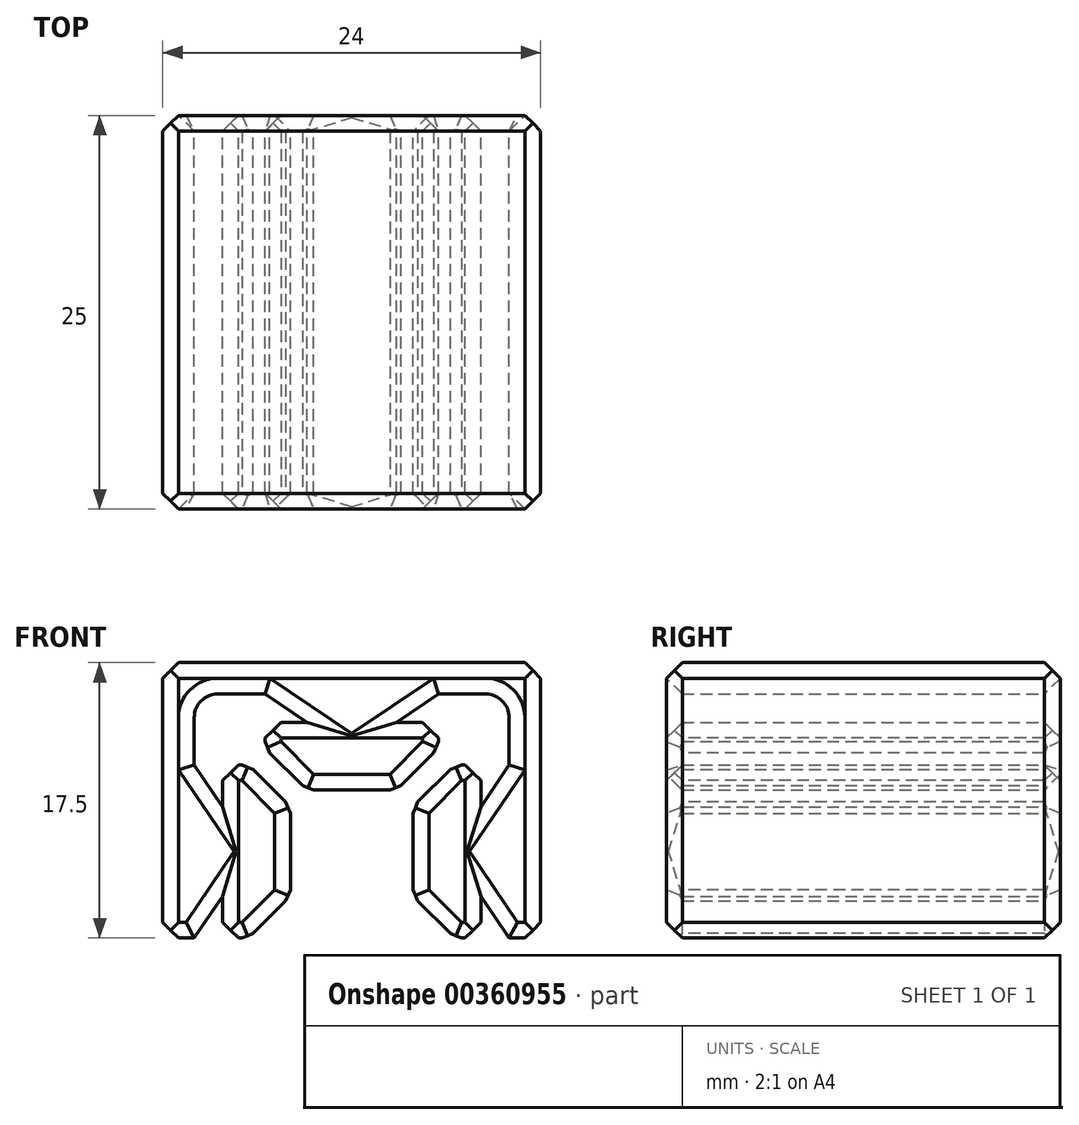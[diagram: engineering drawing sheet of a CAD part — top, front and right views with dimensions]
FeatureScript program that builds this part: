
annotation { "Feature Type Name" : "Feature", "Feature Type Description" : "" }
export const myFeature = defineFeature(function(context is Context, id is Id, definition is map)
    precondition{}
    {
        {
            var Q0;
            Q0=qCreatedBy(makeId("Front.planeOp"),FACE);
            var sketch = newSketch(context, id + "F0", { "sketchPlane" : qUnion([Q0])});
            skLineSegment(sketch, "E0", {"start": v(-8.2, 11) * mm, "end": v(-6.56, 11) * mm});
            skLineSegment(sketch, "E1", {"start": v(-6.56, 11) * mm, "end": v(-3.9, 8.34) * mm});
            skLineSegment(sketch, "E2", {"start": v(-3.9, 8.34) * mm, "end": v(-3.9, 2.66) * mm});
            skLineSegment(sketch, "E3", {"start": v(-3.9, 2.66) * mm, "end": v(-6.56, 0) * mm});
            skLineSegment(sketch, "E4", {"start": v(-6.56, 0) * mm, "end": v(-8.2, 0) * mm});
            skLineSegment(sketch, "E5", {"start": v(-8.2, 8.34) * mm, "end": v(-10, 11) * mm});
            skLineSegment(sketch, "E6", {"start": v(-8.2, 8.34) * mm, "end": v(-8.2, 11) * mm});
            skLineSegment(sketch, "E7", {"start": v(-8.2, 0) * mm, "end": v(-8.2, 2.66) * mm});
            skLineSegment(sketch, "E8", {"start": v(-8.2, 2.66) * mm, "end": v(-10, 0) * mm});
            skLineSegment(sketch, "E9.MirrorCS", {"start": v(8.2, 11) * mm, "end": v(6.56, 11) * mm});
            skLineSegment(sketch, "E10.MirrorCS", {"start": v(3.9, 8.34) * mm, "end": v(3.9, 2.66) * mm});
            skLineSegment(sketch, "E11.MirrorCS", {"start": v(8.2, 8.34) * mm, "end": v(10, 11) * mm});
            skLineSegment(sketch, "E12.MirrorCS", {"start": v(6.56, 0) * mm, "end": v(8.2, 0) * mm});
            skLineSegment(sketch, "E13.MirrorCS", {"start": v(3.9, 2.66) * mm, "end": v(6.56, 0) * mm});
            skLineSegment(sketch, "E14.MirrorCS", {"start": v(8.2, 0) * mm, "end": v(8.2, 2.66) * mm});
            skLineSegment(sketch, "E15.MirrorCS", {"start": v(6.56, 11) * mm, "end": v(3.9, 8.34) * mm});
            skLineSegment(sketch, "E16.MirrorCS", {"start": v(8.2, 8.34) * mm, "end": v(8.2, 11) * mm});
            skLineSegment(sketch, "E17.MirrorCS", {"start": v(8.2, 2.66) * mm, "end": v(10, 0) * mm});
            skLineSegment(sketch, "E18.MirrorCS", {"start": v(-5.5, 13.7) * mm, "end": v(-5.5, 12.06) * mm});
            skLineSegment(sketch, "E19.MirrorCS", {"start": v(-2.84, 9.4) * mm, "end": v(2.84, 9.4) * mm});
            skLineSegment(sketch, "E20.MirrorCS", {"start": v(-2.84, 13.7) * mm, "end": v(-5.5, 15.5) * mm});
            skLineSegment(sketch, "E21.MirrorCS", {"start": v(5.5, 12.06) * mm, "end": v(5.5, 13.7) * mm});
            skLineSegment(sketch, "E22.MirrorCS", {"start": v(2.84, 9.4) * mm, "end": v(5.5, 12.06) * mm});
            skLineSegment(sketch, "E23.MirrorCS", {"start": v(5.5, 13.7) * mm, "end": v(2.84, 13.7) * mm});
            skLineSegment(sketch, "E24.MirrorCS", {"start": v(-5.5, 12.06) * mm, "end": v(-2.84, 9.4) * mm});
            skLineSegment(sketch, "E25.MirrorCS", {"start": v(-2.84, 13.7) * mm, "end": v(-5.5, 13.7) * mm});
            skLineSegment(sketch, "E26.MirrorCS", {"start": v(2.84, 13.7) * mm, "end": v(5.5, 15.5) * mm});
            skPoint(sketch, "E27", {"position": v(0, 9.4) * mm});
            skPoint(sketch, "E28", {"position": v(0, 15.5) * mm});
            skLineSegment(sketch, "E29", {"start": v(-5.5, 15.5) * mm, "end": v(-8.5, 15.5) * mm});
            skLineSegment(sketch, "E30", {"start": v(-10, 14) * mm, "end": v(-10, 11) * mm});
            skLineSegment(sketch, "E31", {"start": v(5.5, 15.5) * mm, "end": v(8.5, 15.5) * mm});
            skLineSegment(sketch, "E32", {"start": v(10, 14) * mm, "end": v(10, 11) * mm});
            skPoint(sketch, "E33.visualSharp", {"position": v(-10, 15.5) * mm});
            skArc(sketch, "E33.filletArc", {"start": v(-8.5, 15.5) * mm, "mid": v(-9.56, 15.06) * mm, "end": v(-10, 14) * mm});
            skPoint(sketch, "E34.visualSharp", {"position": v(10, 15.5) * mm});
            skArc(sketch, "E34.filletArc", {"start": v(10, 14) * mm, "mid": v(9.56, 15.06) * mm, "end": v(8.5, 15.5) * mm});
            skLineSegment(sketch, "E35", {"start": v(-10, 0) * mm, "end": v(-12, 0) * mm});
            skLineSegment(sketch, "E36", {"start": v(-12, 0) * mm, "end": v(-12, 16) * mm});
            skLineSegment(sketch, "E37", {"start": v(-10.5, 17.5) * mm, "end": v(10.5, 17.5) * mm});
            skLineSegment(sketch, "E38", {"start": v(12, 16) * mm, "end": v(12, 0) * mm});
            skLineSegment(sketch, "E39", {"start": v(12, 0) * mm, "end": v(10, 0) * mm});
            skPoint(sketch, "E40.visualSharp", {"position": v(-12, 17.5) * mm});
            skPoint(sketch, "E41.visualSharp", {"position": v(12, 17.5) * mm});
            skLineSegment(sketch, "E42", {"start": v(-12, 16) * mm, "end": v(-12, 17.5) * mm});
            skLineSegment(sketch, "E43", {"start": v(-10.5, 17.5) * mm, "end": v(-12, 17.5) * mm});
            skLineSegment(sketch, "E44", {"start": v(10.5, 17.5) * mm, "end": v(12, 17.5) * mm});
            skLineSegment(sketch, "E45", {"start": v(12, 16) * mm, "end": v(12, 17.5) * mm});
            skSolve(sketch);
        }
        {
            var Q0;
            Q0=qSketchRegion(id+"F0",true);
            extrude(context, id + "F1", {"entities" : qUnion([Q0]), "depth" : 25 * mm});
        }
        {
            var Q0;
            Q0=makeQuery(id+"F1.opExtrude","CAP_FACE",FACE,{"disambiguationData":[OSD([sQuery(id+"F0.wireOp",EDGE,"E0"),sQuery(id+"F0.wireOp",EDGE,"E1"),sQuery(id+"F0.wireOp",EDGE,"E2"),sQuery(id+"F0.wireOp",EDGE,"E3"),sQuery(id+"F0.wireOp",EDGE,"E4"),sQuery(id+"F0.wireOp",EDGE,"E5"),sQuery(id+"F0.wireOp",EDGE,"E6"),sQuery(id+"F0.wireOp",EDGE,"E7"),sQuery(id+"F0.wireOp",EDGE,"E8"),sQuery(id+"F0.wireOp",EDGE,"E9.MirrorCS"),sQuery(id+"F0.wireOp",EDGE,"E10.MirrorCS"),sQuery(id+"F0.wireOp",EDGE,"E11.MirrorCS"),sQuery(id+"F0.wireOp",EDGE,"E12.MirrorCS"),sQuery(id+"F0.wireOp",EDGE,"E13.MirrorCS"),sQuery(id+"F0.wireOp",EDGE,"E14.MirrorCS"),sQuery(id+"F0.wireOp",EDGE,"E15.MirrorCS"),sQuery(id+"F0.wireOp",EDGE,"E16.MirrorCS"),sQuery(id+"F0.wireOp",EDGE,"E17.MirrorCS"),sQuery(id+"F0.wireOp",EDGE,"E18.MirrorCS"),sQuery(id+"F0.wireOp",EDGE,"E19.MirrorCS"),sQuery(id+"F0.wireOp",EDGE,"E20.MirrorCS"),sQuery(id+"F0.wireOp",EDGE,"E21.MirrorCS"),sQuery(id+"F0.wireOp",EDGE,"E22.MirrorCS"),sQuery(id+"F0.wireOp",EDGE,"E23.MirrorCS"),sQuery(id+"F0.wireOp",EDGE,"E24.MirrorCS"),sQuery(id+"F0.wireOp",EDGE,"E25.MirrorCS"),sQuery(id+"F0.wireOp",EDGE,"E26.MirrorCS"),sQuery(id+"F0.wireOp",EDGE,"E29"),sQuery(id+"F0.wireOp",EDGE,"E30"),sQuery(id+"F0.wireOp",EDGE,"E31"),sQuery(id+"F0.wireOp",EDGE,"E32"),sQuery(id+"F0.wireOp",EDGE,"E33.filletArc"),sQuery(id+"F0.wireOp",EDGE,"E34.filletArc"),sQuery(id+"F0.wireOp",EDGE,"E35"),sQuery(id+"F0.wireOp",EDGE,"E36"),sQuery(id+"F0.wireOp",EDGE,"E37"),sQuery(id+"F0.wireOp",EDGE,"E38"),sQuery(id+"F0.wireOp",EDGE,"E39"),sQuery(id+"F0.wireOp",EDGE,"E40.filletArc"),sQuery(id+"F0.wireOp",EDGE,"E41.filletArc")])],"isStart":false});
            var Q1;
            Q1=makeQuery(id+"F1.opExtrude","CAP_FACE",FACE,{"disambiguationData":[OSD([sQuery(id+"F0.wireOp",EDGE,"E0"),sQuery(id+"F0.wireOp",EDGE,"E1"),sQuery(id+"F0.wireOp",EDGE,"E2"),sQuery(id+"F0.wireOp",EDGE,"E3"),sQuery(id+"F0.wireOp",EDGE,"E4"),sQuery(id+"F0.wireOp",EDGE,"E5"),sQuery(id+"F0.wireOp",EDGE,"E6"),sQuery(id+"F0.wireOp",EDGE,"E7"),sQuery(id+"F0.wireOp",EDGE,"E8"),sQuery(id+"F0.wireOp",EDGE,"E9.MirrorCS"),sQuery(id+"F0.wireOp",EDGE,"E10.MirrorCS"),sQuery(id+"F0.wireOp",EDGE,"E11.MirrorCS"),sQuery(id+"F0.wireOp",EDGE,"E12.MirrorCS"),sQuery(id+"F0.wireOp",EDGE,"E13.MirrorCS"),sQuery(id+"F0.wireOp",EDGE,"E14.MirrorCS"),sQuery(id+"F0.wireOp",EDGE,"E15.MirrorCS"),sQuery(id+"F0.wireOp",EDGE,"E16.MirrorCS"),sQuery(id+"F0.wireOp",EDGE,"E17.MirrorCS"),sQuery(id+"F0.wireOp",EDGE,"E18.MirrorCS"),sQuery(id+"F0.wireOp",EDGE,"E19.MirrorCS"),sQuery(id+"F0.wireOp",EDGE,"E20.MirrorCS"),sQuery(id+"F0.wireOp",EDGE,"E21.MirrorCS"),sQuery(id+"F0.wireOp",EDGE,"E22.MirrorCS"),sQuery(id+"F0.wireOp",EDGE,"E23.MirrorCS"),sQuery(id+"F0.wireOp",EDGE,"E24.MirrorCS"),sQuery(id+"F0.wireOp",EDGE,"E25.MirrorCS"),sQuery(id+"F0.wireOp",EDGE,"E26.MirrorCS"),sQuery(id+"F0.wireOp",EDGE,"E29"),sQuery(id+"F0.wireOp",EDGE,"E30"),sQuery(id+"F0.wireOp",EDGE,"E31"),sQuery(id+"F0.wireOp",EDGE,"E32"),sQuery(id+"F0.wireOp",EDGE,"E33.filletArc"),sQuery(id+"F0.wireOp",EDGE,"E34.filletArc"),sQuery(id+"F0.wireOp",EDGE,"E35"),sQuery(id+"F0.wireOp",EDGE,"E36"),sQuery(id+"F0.wireOp",EDGE,"E37"),sQuery(id+"F0.wireOp",EDGE,"E38"),sQuery(id+"F0.wireOp",EDGE,"E39"),sQuery(id+"F0.wireOp",EDGE,"E40.filletArc"),sQuery(id+"F0.wireOp",EDGE,"E41.filletArc")])],"isStart":true});
            chamfer(context, id + "F2", {"entities" : qUnion([Q0, Q1]), "width" : 1 * mm, "tangentPropagation" : true});
        }
        {
            var Q0;
            Q0=makeQuery(id+"F1.opExtrude","SWEPT_EDGE",EDGE,{"disambiguationData":[OSD([sQuery(id+"F0.wireOp",EDGE,"E44"),sQuery(id+"F0.wireOp",EDGE,"E45")])]});
            var Q1;
            Q1=makeQuery(id+"F1.opExtrude","SWEPT_EDGE",EDGE,{"disambiguationData":[OSD([sQuery(id+"F0.wireOp",EDGE,"E42"),sQuery(id+"F0.wireOp",EDGE,"E43")])]});
            var Q2;
            Q2=makeQuery(id+"F1.opExtrude","SWEPT_EDGE",EDGE,{"disambiguationData":[OSD([sQuery(id+"F0.wireOp",EDGE,"E35"),sQuery(id+"F0.wireOp",EDGE,"E36")])]});
            var Q3;
            Q3=makeQuery(id+"F1.opExtrude","SWEPT_EDGE",EDGE,{"disambiguationData":[OSD([sQuery(id+"F0.wireOp",EDGE,"E38"),sQuery(id+"F0.wireOp",EDGE,"E39")])]});
            var Q4;
            Q4=makeQuery(id+"F1.opExtrude","SWEPT_EDGE",EDGE,{"disambiguationData":[OSD([sQuery(id+"F0.wireOp",EDGE,"E10.MirrorCS"),sQuery(id+"F0.wireOp",EDGE,"E13.MirrorCS")])]});
            var Q5;
            Q5=makeQuery(id+"F1.opExtrude","SWEPT_EDGE",EDGE,{"disambiguationData":[OSD([sQuery(id+"F0.wireOp",EDGE,"E10.MirrorCS"),sQuery(id+"F0.wireOp",EDGE,"E15.MirrorCS")])]});
            var Q6;
            Q6=makeQuery(id+"F1.opExtrude","SWEPT_EDGE",EDGE,{"disambiguationData":[OSD([sQuery(id+"F0.wireOp",EDGE,"E19.MirrorCS"),sQuery(id+"F0.wireOp",EDGE,"E24.MirrorCS")])]});
            var Q7;
            Q7=makeQuery(id+"F1.opExtrude","SWEPT_EDGE",EDGE,{"disambiguationData":[OSD([sQuery(id+"F0.wireOp",EDGE,"E19.MirrorCS"),sQuery(id+"F0.wireOp",EDGE,"E22.MirrorCS")])]});
            var Q8;
            Q8=makeQuery(id+"F1.opExtrude","SWEPT_EDGE",EDGE,{"disambiguationData":[OSD([sQuery(id+"F0.wireOp",EDGE,"E1"),sQuery(id+"F0.wireOp",EDGE,"E2")])]});
            var Q9;
            Q9=makeQuery(id+"F1.opExtrude","SWEPT_EDGE",EDGE,{"disambiguationData":[OSD([sQuery(id+"F0.wireOp",EDGE,"E2"),sQuery(id+"F0.wireOp",EDGE,"E3")])]});
            var Q10;
            Q10=makeQuery(id+"F1.opExtrude","SWEPT_EDGE",EDGE,{"disambiguationData":[OSD([sQuery(id+"F0.wireOp",EDGE,"E3"),sQuery(id+"F0.wireOp",EDGE,"E4")])]});
            var Q11;
            Q11=makeQuery(id+"F1.opExtrude","SWEPT_EDGE",EDGE,{"disambiguationData":[OSD([sQuery(id+"F0.wireOp",EDGE,"E0"),sQuery(id+"F0.wireOp",EDGE,"E1")])]});
            var Q12;
            Q12=makeQuery(id+"F1.opExtrude","SWEPT_EDGE",EDGE,{"disambiguationData":[OSD([sQuery(id+"F0.wireOp",EDGE,"E18.MirrorCS"),sQuery(id+"F0.wireOp",EDGE,"E24.MirrorCS")])]});
            var Q13;
            Q13=makeQuery(id+"F1.opExtrude","SWEPT_EDGE",EDGE,{"disambiguationData":[OSD([sQuery(id+"F0.wireOp",EDGE,"E21.MirrorCS"),sQuery(id+"F0.wireOp",EDGE,"E22.MirrorCS")])]});
            var Q14;
            Q14=makeQuery(id+"F1.opExtrude","SWEPT_EDGE",EDGE,{"disambiguationData":[OSD([sQuery(id+"F0.wireOp",EDGE,"E9.MirrorCS"),sQuery(id+"F0.wireOp",EDGE,"E15.MirrorCS")])]});
            var Q15;
            Q15=makeQuery(id+"F1.opExtrude","SWEPT_EDGE",EDGE,{"disambiguationData":[OSD([sQuery(id+"F0.wireOp",EDGE,"E12.MirrorCS"),sQuery(id+"F0.wireOp",EDGE,"E13.MirrorCS")])]});
            var Q16;
            Q16=makeQuery(id+"F1.opExtrude","SWEPT_EDGE",EDGE,{"disambiguationData":[OSD([sQuery(id+"F0.wireOp",EDGE,"E12.MirrorCS"),sQuery(id+"F0.wireOp",EDGE,"E14.MirrorCS")])]});
            var Q17;
            Q17=makeQuery(id+"F1.opExtrude","SWEPT_EDGE",EDGE,{"disambiguationData":[OSD([sQuery(id+"F0.wireOp",EDGE,"E9.MirrorCS"),sQuery(id+"F0.wireOp",EDGE,"E16.MirrorCS")])]});
            var Q18;
            Q18=makeQuery(id+"F1.opExtrude","SWEPT_EDGE",EDGE,{"disambiguationData":[OSD([sQuery(id+"F0.wireOp",EDGE,"E21.MirrorCS"),sQuery(id+"F0.wireOp",EDGE,"E23.MirrorCS")])]});
            var Q19;
            Q19=makeQuery(id+"F1.opExtrude","SWEPT_EDGE",EDGE,{"disambiguationData":[OSD([sQuery(id+"F0.wireOp",EDGE,"E18.MirrorCS"),sQuery(id+"F0.wireOp",EDGE,"E25.MirrorCS")])]});
            var Q20;
            Q20=makeQuery(id+"F1.opExtrude","SWEPT_EDGE",EDGE,{"disambiguationData":[OSD([sQuery(id+"F0.wireOp",EDGE,"E0"),sQuery(id+"F0.wireOp",EDGE,"E6")])]});
            var Q21;
            Q21=makeQuery(id+"F1.opExtrude","SWEPT_EDGE",EDGE,{"disambiguationData":[OSD([sQuery(id+"F0.wireOp",EDGE,"E4"),sQuery(id+"F0.wireOp",EDGE,"E7")])]});
            chamfer(context, id + "F3", {"entities" : qUnion([Q0, Q1, Q2, Q3, Q4, Q5, Q6, Q7, Q8, Q9, Q10, Q11, Q12, Q13, Q14, Q15, Q16, Q17, Q18, Q19, Q20, Q21]), "width" : 1 * mm, "tangentPropagation" : true});
        }
    });
